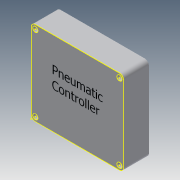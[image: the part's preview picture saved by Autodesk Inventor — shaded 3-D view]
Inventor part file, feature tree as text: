
AUTODESK INVENTOR PART (.ipt)
format: ipt  version: 2014 (Build 180170000, 170)  size: 102,912 bytes
history: native  units: in
note: dims shown in document units (in); Inventor stores cm internally (conversion verified against a paired STEP export)
features: sketch x3, extrude x1, fillet x1, hole x1
ambient origin geometry x8: Origin, YZ Plane, XZ Plane, XY Plane, X Axis, Y Axis, Z Axis, Center Point
bodies: Solid1 (feature_tree)
feature tree (6):
  extrude  "Extrusion1"  Depth=2.5in
  fillet  "Fillet1"  Radius=0.75in
  hole  "Hole1"  [1 undecoded]
  sketch  "Sketch3"  dims[d5=0.156in d6=0.75in d7=0.375in d8=0.25in d9=0.5635in d10=1.0in d11=0.8108in]
  sketch  "Sketch1"  dims[d0=2.75in d1=2.5in d2=0.75in d3=0.0in]
  sketch  "Sketch2"  dims[d4=0.125in]
note: 1 required parameter value undecoded (feature->parameter linkage not recoverable at this tier; creation-order binding heuristic only, values carry confidence <= 0.55)
